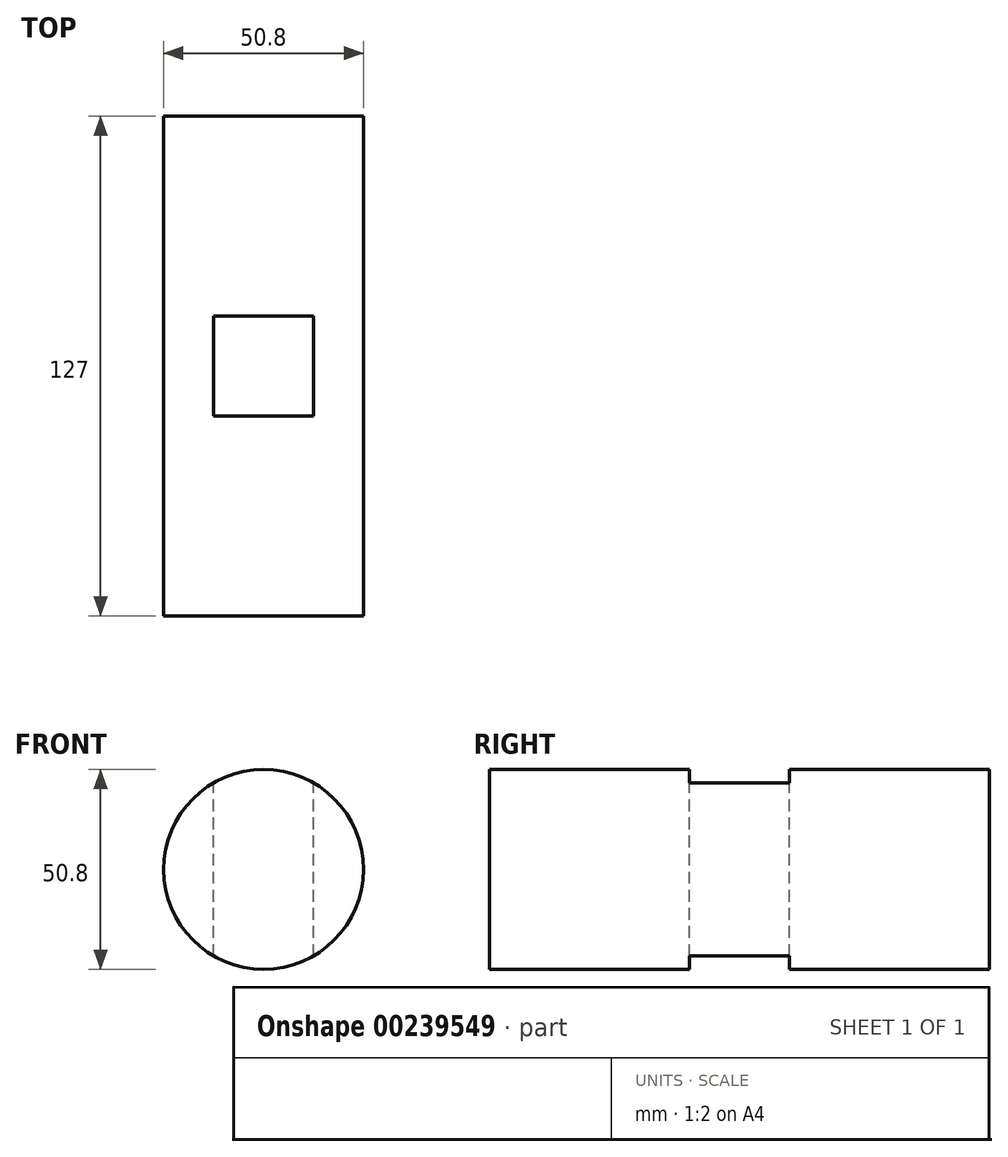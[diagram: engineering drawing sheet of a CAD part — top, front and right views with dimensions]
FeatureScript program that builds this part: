
annotation { "Feature Type Name" : "Feature", "Feature Type Description" : "" }
export const myFeature = defineFeature(function(context is Context, id is Id, definition is map)
    precondition{}
    {
        {
            var Q0;
            Q0=qCreatedBy(makeId("Front.planeOp"),FACE);
            var sketch = newSketch(context, id + "F0", { "sketchPlane" : qUnion([Q0])});
            skCircle(sketch, "E0", {"center": v(0, 0) * mm, "radius": 25.4 * mm});
            skSolve(sketch);
        }
        {
            var Q0;
            Q0 = qSketchRegion(id + "F0", true);
            extrude(context, id + "F1", {"entities" : qUnion([Q0]), "endBound" : BoundingType.SYMMETRIC, "depth" : 127 * mm});
        }
        {
            var Q0;
            Q0=qCreatedBy(makeId("Top.planeOp"),FACE);
            var sketch = newSketch(context, id + "F2", { "sketchPlane" : qUnion([Q0])});
            skLineSegment(sketch, "E1.bottom", {"start": v(12.7, -12.7) * mm, "end": v(-12.7, -12.7) * mm});
            skLineSegment(sketch, "E1.top", {"start": v(12.7, 12.7) * mm, "end": v(-12.7, 12.7) * mm});
            skLineSegment(sketch, "E1.left", {"start": v(12.7, -12.7) * mm, "end": v(12.7, 12.7) * mm});
            skLineSegment(sketch, "E1.right", {"start": v(-12.7, -12.7) * mm, "end": v(-12.7, 12.7) * mm});
            skPoint(sketch, "E1.middle", {"position": v(0, 0) * mm});
            skSolve(sketch);
        }
        {
            var Q0;
            Q0 = qSketchRegion(id + "F2", true);
            extrude(context, id + "F3", {"entities" : qUnion([Q0]), "operationType" : NewBodyOperationType.REMOVE, "endBound" : BoundingType.SYMMETRIC, "oppositeDirection" : true, "depth" : 66.04 * mm});
        }
    });
